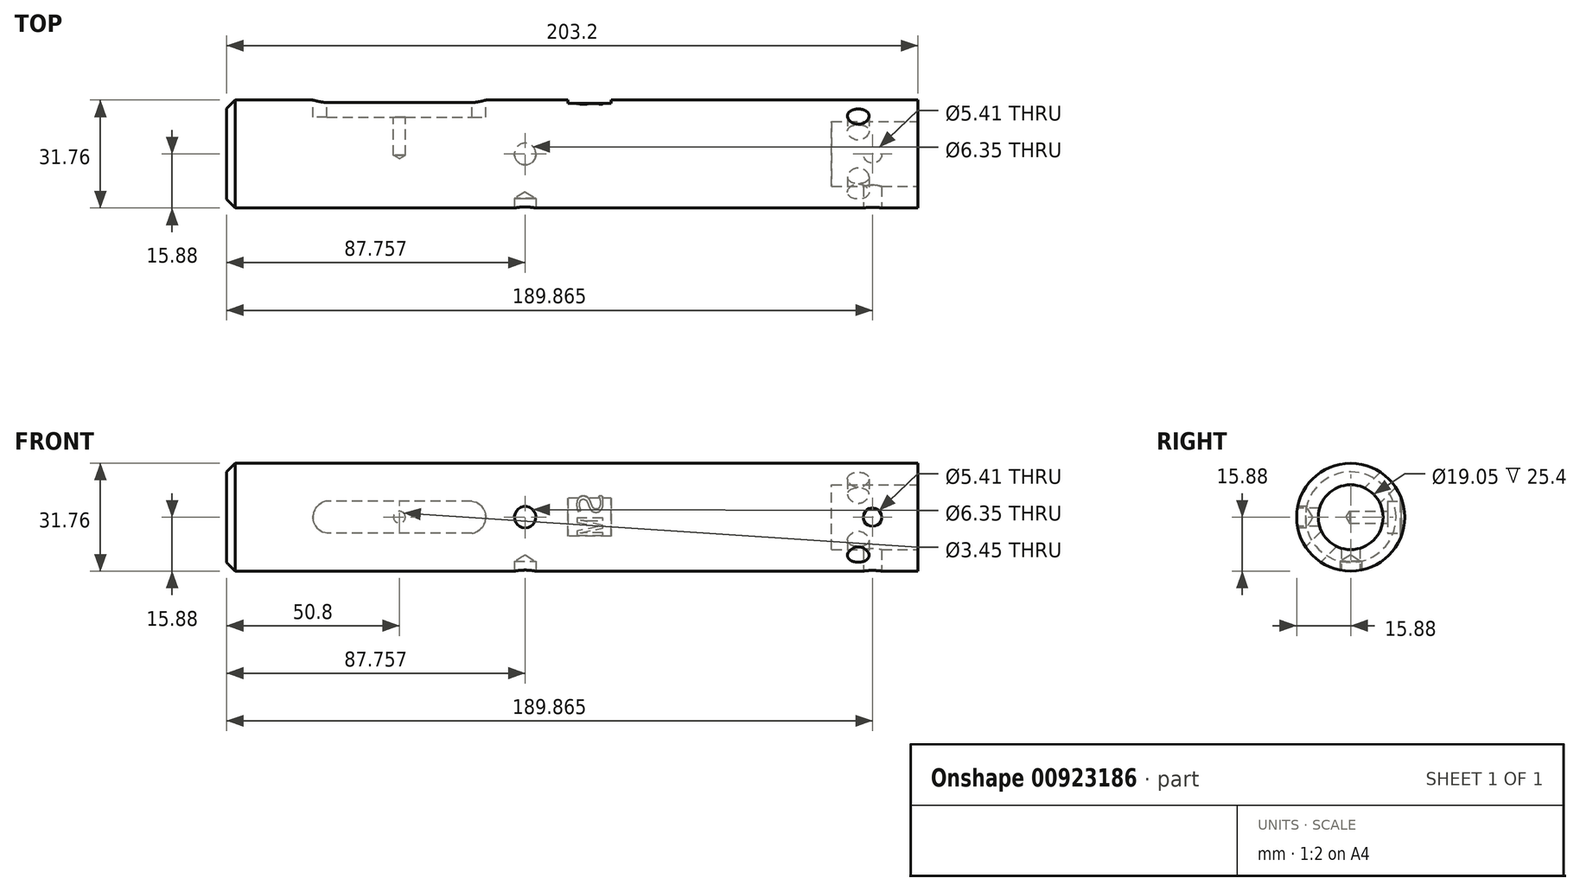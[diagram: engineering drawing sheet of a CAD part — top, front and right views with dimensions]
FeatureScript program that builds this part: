
annotation { "Feature Type Name" : "Feature", "Feature Type Description" : "" }
export const myFeature = defineFeature(function(context is Context, id is Id, definition is map)
    precondition{}
    {
        {
            var Q0;
            Q0=qCreatedBy(makeId("Right.planeOp"),FACE);
            var sketch = newSketch(context, id + "F0", { "sketchPlane" : qUnion([Q0])});
            skCircle(sketch, "E0", {"center": v(0, 0) * mm, "radius": 15.88 * mm});
            skSolve(sketch);
        }
        {
            var Q0;
            Q0 = qSketchRegion(id + "F0", true);
            extrude(context, id + "F1", {"entities" : qUnion([Q0]), "depth" : 203.2 * mm, "offsetDistance" : 25.4 * mm});
        }
        {
            var Q0;
            Q0=qCreatedBy(makeId("Front.planeOp"),FACE);
            cPlane(context, id + "F2", {"entities" : qUnion([Q0]), "cplaneType" : CPlaneType.OFFSET, "offset" : 15.88 * mm, "oppositeDirection" : true, "width" : 152.4 * mm, "height" : 152.4 * mm});
        }
        {
            var Q0;
            Q0=qCreatedBy(id+"F2.planeOp",FACE);
            var sketch = newSketch(context, id + "F3", { "sketchPlane" : qUnion([Q0])});
            skLineSegment(sketch, "E1.bottom", {"start": v(29.52, 4.74) * mm, "end": v(72.08, 4.74) * mm});
            skLineSegment(sketch, "E1.top", {"start": v(29.52, -4.74) * mm, "end": v(72.08, -4.74) * mm});
            skPoint(sketch, "E1.middle", {"position": v(50.8, 0) * mm});
            skArc(sketch, "E2", {"start": v(29.52, 4.74) * mm, "mid": v(25.4, 0) * mm, "end": v(29.52, -4.74) * mm});
            skArc(sketch, "E3", {"start": v(72.08, -4.74) * mm, "mid": v(76.2, 0) * mm, "end": v(72.08, 4.74) * mm});
            skSolve(sketch);
        }
        {
            var Q0;
            Q0=makeQuery(id+"F3.imprint","IMPRINT",FACE,{"disambiguationData":[TD([[makeQuery(id+"F3.imprint","IMPRINT",EDGE,{"derivedFrom":sQuery(id+"F3.wireOp",EDGE,"E1.bottom")}),-1.0]])]});
            extrude(context, id + "F4", {"entities" : qUnion([Q0]), "operationType" : NewBodyOperationType.REMOVE, "depth" : 5.08 * mm, "offsetDistance" : 25.4 * mm});
        }
        {
            var Q0;
            Q0=makeQuery(id+"F4.boolean.opBoolean","COPY",FACE,{"derivedFrom":makeQuery(id+"F4.opExtrude","CAP_FACE",FACE,{"disambiguationData":[OSD([sQuery(id+"F3.wireOp",EDGE,"E1.bottom"),sQuery(id+"F3.wireOp",EDGE,"E1.top"),sQuery(id+"F3.wireOp",EDGE,"E2"),sQuery(id+"F3.wireOp",EDGE,"E3")])],"isStart":false})});
            var sketch = newSketch(context, id + "F5", { "sketchPlane" : qUnion([Q0])});
            skCircle(sketch, "E4", {"center": v(-50.8, 0) * mm, "radius": 2.41 * mm});
            skSolve(sketch);
        }
        {
            var Q0;
            Q0=qCreatedBy(makeId("Top.planeOp"),FACE);
            cPlane(context, id + "F6", {"entities" : qUnion([Q0]), "cplaneType" : CPlaneType.OFFSET, "offset" : 15.88 * mm, "oppositeDirection" : true, "width" : 152.4 * mm, "height" : 152.4 * mm});
        }
        {
            var Q0;
            Q0=qCreatedBy(id+"F6.planeOp",FACE);
            var sketch = newSketch(context, id + "F7", { "sketchPlane" : qUnion([Q0])});
            skCircle(sketch, "E5", {"center": v(189.87, 0) * mm, "radius": 3.18 * mm});
            skCircle(sketch, "E6", {"center": v(87.76, 0) * mm, "radius": 3.18 * mm});
            skSolve(sketch);
        }
        {
            var Q0;
            Q0=makeQuery(id+"F1.opExtrude","CAP_FACE",FACE,{"disambiguationData":[OSD([sQuery(id+"F0.wireOp",EDGE,"E0")])],"isStart":false});
            var sketch = newSketch(context, id + "F8", { "sketchPlane" : qUnion([Q0])});
            skLineSegment(sketch, "E7", {"start": v(0, -15.88) * mm, "end": v(-15.88, 0) * mm, "construction": true});
            skSolve(sketch);
        }
        {
            var Q0;
            Q0=sQuery(id+"F8.wireOp",EDGE,"E7");
            cPlane(context, id + "F9", {"entities" : qUnion([Q0]), "cplaneType" : CPlaneType.LINE_ANGLE, "offset" : 25.4 * mm, "angle" : 0 * degree, "width" : 152.4 * mm, "height" : 152.4 * mm});
        }
        {
            var Q0;
            Q0=qCreatedBy(id+"F9.planeOp",FACE);
            var sketch = newSketch(context, id + "F10", { "sketchPlane" : qUnion([Q0])});
            skCircle(sketch, "E8", {"center": v(185.67, 0) * mm, "radius": 3.18 * mm});
            skSolve(sketch);
        }
        {
            var Q0;
            Q0=makeQuery(id+"F8.imprint","IMPRINT",FACE,{"disambiguationData":[TD([[makeQuery(id+"F8.imprint","IMPRINT",EDGE,{"derivedFrom":makeQuery(id+"F1.opExtrude","CAP_EDGE",EDGE,{"disambiguationData":[OSD([sQuery(id+"F0.wireOp",EDGE,"E0")])],"isStart":false})}),1.0]])]});
            var sketch = newSketch(context, id + "F11", { "sketchPlane" : qUnion([Q0])});
            skCircle(sketch, "E9", {"center": v(0, 0) * mm, "radius": 9.53 * mm});
            skSolve(sketch);
        }
        {
            var Q0;
            Q0 = qSketchRegion(id + "F11", true);
            extrude(context, id + "F12", {"entities" : qUnion([Q0]), "operationType" : NewBodyOperationType.REMOVE, "oppositeDirection" : true, "depth" : 25.4 * mm, "offsetDistance" : 25.4 * mm});
        }
        {
            var Q0;
            Q0=qCreatedBy(id+"F2.planeOp",FACE);
            var sketch = newSketch(context, id + "F13", { "sketchPlane" : qUnion([Q0])});
            skLineSegment(sketch, "E10.bottom", {"start": v(112.97, -12.89) * mm, "end": v(100.27, -12.89) * mm});
            skLineSegment(sketch, "E10.top", {"start": v(112.97, 12.89) * mm, "end": v(100.27, 12.89) * mm});
            skLineSegment(sketch, "E10.left", {"start": v(112.97, -12.89) * mm, "end": v(112.97, 12.89) * mm});
            skLineSegment(sketch, "E10.right", {"start": v(100.27, -12.89) * mm, "end": v(100.27, 12.89) * mm});
            skPoint(sketch, "E10.middle", {"position": v(106.62, 0) * mm});
            skSolve(sketch);
        }
        {
            var Q0;
            Q0 = qSketchRegion(id + "F13", true);
            extrude(context, id + "F14", {"entities" : qUnion([Q0]), "operationType" : NewBodyOperationType.REMOVE, "depth" : 1.02 * mm, "offsetDistance" : 25.4 * mm});
        }
        {
            var Q0;
            Q0=makeQuery(id+"F14.boolean.opBoolean","COPY",FACE,{"derivedFrom":makeQuery(id+"F14.opExtrude","CAP_FACE",FACE,{"disambiguationData":[OSD([sQuery(id+"F13.wireOp",EDGE,"E10.bottom"),sQuery(id+"F13.wireOp",EDGE,"E10.top"),sQuery(id+"F13.wireOp",EDGE,"E10.left"),sQuery(id+"F13.wireOp",EDGE,"E10.right")])],"isStart":false})});
            var sketch = newSketch(context, id + "F15", { "sketchPlane" : qUnion([Q0])});
            skText(sketch, "E11", { "text": "M", "fontName": "DroidSansMono.ttf"});
            skText(sketch, "E12", { "text": "S", "fontName": "DroidSansMono.ttf"});
            const initialGuessF15  = {"E11": [-0.11057, 0.00038, 0, -1, 0.00762], "E12": [-0.11057, 0.00706, 0, -1, 0.00762]};
            skSetInitialGuess(sketch, initialGuessF15);
            skSolve(sketch);
        }
        {
            var Q0;
            Q0 = qSketchRegion(id + "F15", true);
            extrude(context, id + "F16", {"entities" : qUnion([Q0]), "operationType" : NewBodyOperationType.REMOVE, "oppositeDirection" : true, "depth" : 0.25 * mm, "offsetDistance" : 25.4 * mm});
        }
        {
            var Q0;
            Q0=qCreatedBy(makeId("Front.planeOp"),FACE);
            cPlane(context, id + "F17", {"entities" : qUnion([Q0]), "cplaneType" : CPlaneType.OFFSET, "offset" : 15.88 * mm, "width" : 152.4 * mm, "height" : 152.4 * mm});
        }
        {
            var Q0;
            Q0=qCreatedBy(id+"F17.planeOp",FACE);
            var sketch = newSketch(context, id + "F18", { "sketchPlane" : qUnion([Q0])});
            skCircle(sketch, "E13", {"center": v(87.76, 0) * mm, "radius": 3.18 * mm});
            skCircle(sketch, "E14", {"center": v(189.87, 0) * mm, "radius": 3.18 * mm});
            skSolve(sketch);
        }
        {
            var Q0;
            Q0=makeQuery(id+"F1.opExtrude","CAP_EDGE",EDGE,{"disambiguationData":[OSD([sQuery(id+"F0.wireOp",EDGE,"E0")])],"isStart":true});
            chamfer(context, id + "F19", {"entities" : qUnion([Q0]), "width" : 2.54 * mm, "tangentPropagation" : true});
        }
        {
            var Q0;
            Q0=sQuery(id+"F18.wireOp",VERTEX,"E14.center");
            var Q1;
            Q1=makeQuery(id+"F1.opExtrude","SWEPT_BODY",BODY,{"disambiguationData":[OSD([sQuery(id+"F0.wireOp",EDGE,"E0")])]});
            hole(context, id + "F20", {"style" : HoleStyle.SIMPLE, "endStyle" : HoleEndStyle.BLIND, "standardTappedOrClearance" : lookupTablePath({ "standard" : "ANSI", "engagement" : "75%", "pitch" : "28 tpi", "size" : "1/4", "type" : "Tapped" }), "standardBlindInLast" : lookupTablePath({ "standard" : "ANSI", "fit" : "Free", "engagement" : "75%", "pitch" : "28 tpi", "size" : "1/4", "type" : "Clearance & tapped" }), "holeDiameter" : 5.4 * mm, "majorDiameter" : 6.35 * mm, "showTappedDepth" : true, "holeDepth" : 12.16 * mm, "isTappedThrough" : true, "tappedDepth" : 7.62 * mm, "tapClearance" : 5, "locations" : qUnion([Q0]), "scope" : qUnion([Q1])});
        }
        {
            var Q0;
            Q0=sQuery(id+"F7.wireOp",VERTEX,"E5.center");
            var Q1;
            Q1=makeQuery(id+"F1.opExtrude","SWEPT_BODY",BODY,{"disambiguationData":[OSD([sQuery(id+"F0.wireOp",EDGE,"E0")])]});
            hole(context, id + "F21", {"style" : HoleStyle.SIMPLE, "endStyle" : HoleEndStyle.BLIND, "oppositeDirection" : true, "standardTappedOrClearance" : lookupTablePath({ "standard" : "ANSI", "engagement" : "75%", "pitch" : "28 tpi", "size" : "1/4", "type" : "Tapped" }), "standardBlindInLast" : lookupTablePath({ "fit" : "Free", "standard" : "ANSI", "engagement" : "75%", "pitch" : "28 tpi", "size" : "1/4", "type" : "Clearance & tapped" }), "holeDiameter" : 5.4 * mm, "majorDiameter" : 6.35 * mm, "showTappedDepth" : true, "holeDepth" : 12.16 * mm, "isTappedThrough" : true, "tappedDepth" : 7.62 * mm, "tapClearance" : 5, "locations" : qUnion([Q0]), "scope" : qUnion([Q1])});
        }
        {
            var Q0;
            Q0=sQuery(id+"F7.wireOp",VERTEX,"E6.center");
            var Q1;
            Q1=makeQuery(id+"F1.opExtrude","SWEPT_BODY",BODY,{"disambiguationData":[OSD([sQuery(id+"F0.wireOp",EDGE,"E0")])]});
            hole(context, id + "F22", {"style" : HoleStyle.SIMPLE, "endStyle" : HoleEndStyle.BLIND, "oppositeDirection" : true, "holeDiameter" : 6.35 * mm, "majorDiameter" : 6.35 * mm, "holeDepth" : 2.54 * mm, "isTappedThrough" : true, "tappedDepth" : 7.62 * mm, "tapClearance" : 5, "locations" : qUnion([Q0]), "scope" : qUnion([Q1])});
        }
        {
            var Q0;
            Q0=sQuery(id+"F18.wireOp",VERTEX,"E13.center");
            var Q1;
            Q1=makeQuery(id+"F1.opExtrude","SWEPT_BODY",BODY,{"disambiguationData":[OSD([sQuery(id+"F0.wireOp",EDGE,"E0")])]});
            hole(context, id + "F23", {"style" : HoleStyle.SIMPLE, "endStyle" : HoleEndStyle.BLIND, "holeDiameter" : 6.35 * mm, "majorDiameter" : 6.35 * mm, "holeDepth" : 2.54 * mm, "isTappedThrough" : true, "tappedDepth" : 7.62 * mm, "tapClearance" : 5, "locations" : qUnion([Q0]), "scope" : qUnion([Q1])});
        }
        {
            var Q0;
            Q0=qCreatedBy(id+"F9.planeOp",FACE);
            cPlane(context, id + "F24", {"entities" : qUnion([Q0]), "cplaneType" : CPlaneType.OFFSET, "offset" : 4.67 * mm, "width" : 152.4 * mm, "height" : 152.4 * mm});
        }
        {
            var Q0;
            Q0=qCreatedBy(id+"F24.planeOp",FACE);
            var sketch = newSketch(context, id + "F25", { "sketchPlane" : qUnion([Q0])});
            skPoint(sketch, "E15", {"position": v(185.67, 0) * mm});
            skSolve(sketch);
        }
        {
            var Q0;
            Q0=sQuery(id+"F25.wireOp",VERTEX,"E15");
            var Q1;
            Q1=makeQuery(id+"F1.opExtrude","SWEPT_BODY",BODY,{"disambiguationData":[OSD([sQuery(id+"F0.wireOp",EDGE,"E0")])]});
            hole(context, id + "F26", {"style" : HoleStyle.SIMPLE, "endStyle" : HoleEndStyle.THROUGH, "holeDiameter" : 6.35 * mm, "majorDiameter" : 6.35 * mm, "isTappedThrough" : true, "tappedDepth" : 7.62 * mm, "tapClearance" : 5, "locations" : qUnion([Q0]), "scope" : qUnion([Q1])});
        }
        {
            var Q0;
            Q0=sQuery(id+"F5.wireOp",VERTEX,"E4.center");
            var Q1;
            Q1=makeQuery(id+"F1.opExtrude","SWEPT_BODY",BODY,{"disambiguationData":[OSD([sQuery(id+"F0.wireOp",EDGE,"E0")])]});
            hole(context, id + "F27", {"style" : HoleStyle.SIMPLE, "endStyle" : HoleEndStyle.BLIND, "standardTappedOrClearance" : lookupTablePath({ "standard" : "ANSI", "engagement" : "75%", "pitch" : "36 tpi", "size" : "#8", "type" : "Tapped" }), "standardBlindInLast" : lookupTablePath({ "standard" : "ANSI", "fit" : "Free", "engagement" : "75%", "pitch" : "36 tpi", "size" : "#8", "type" : "Clearance & tapped" }), "holeDiameter" : 3.45 * mm, "majorDiameter" : 4.17 * mm, "showTappedDepth" : true, "holeDepth" : 11.15 * mm, "isTappedThrough" : true, "tappedDepth" : 7.62 * mm, "tapClearance" : 5, "locations" : qUnion([Q0]), "scope" : qUnion([Q1])});
        }
    });
